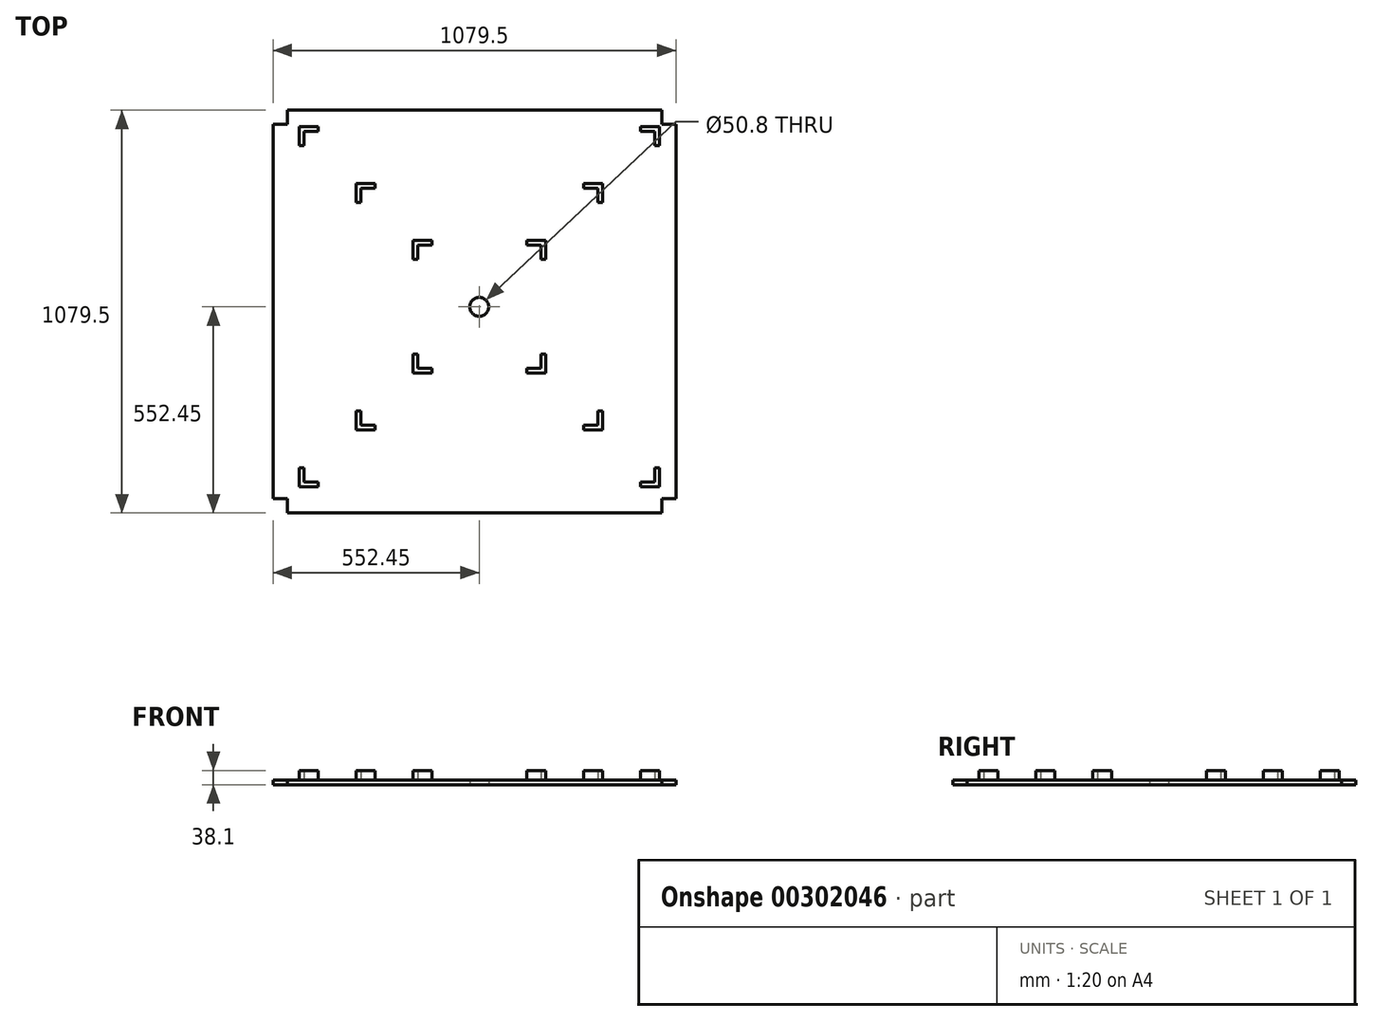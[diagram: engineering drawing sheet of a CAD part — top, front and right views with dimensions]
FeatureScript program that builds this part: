
annotation { "Feature Type Name" : "Feature", "Feature Type Description" : "" }
export const myFeature = defineFeature(function(context is Context, id is Id, definition is map)
    precondition{}
    {
        {
            var Q0;
            Q0=qCreatedBy(makeId("Top.planeOp"),FACE);
            var sketch = newSketch(context, id + "F0", { "sketchPlane" : qUnion([Q0])});
            skLineSegment(sketch, "E0", {"start": v(-552.45, 488.95) * mm, "end": v(-552.45, -514.35) * mm});
            skLineSegment(sketch, "E1", {"start": v(-552.45, -514.35) * mm, "end": v(-514.35, -514.35) * mm});
            skLineSegment(sketch, "E2", {"start": v(-514.35, -514.35) * mm, "end": v(-514.35, -552.45) * mm});
            skLineSegment(sketch, "E3", {"start": v(-514.35, -552.45) * mm, "end": v(488.95, -552.45) * mm});
            skLineSegment(sketch, "E4", {"start": v(488.95, -552.45) * mm, "end": v(488.95, -514.35) * mm});
            skLineSegment(sketch, "E5", {"start": v(488.95, -514.35) * mm, "end": v(527.05, -514.35) * mm});
            skLineSegment(sketch, "E6", {"start": v(527.05, -514.35) * mm, "end": v(527.05, 488.95) * mm});
            skLineSegment(sketch, "E7", {"start": v(527.05, 488.95) * mm, "end": v(488.95, 488.95) * mm});
            skLineSegment(sketch, "E8", {"start": v(488.95, 488.95) * mm, "end": v(488.95, 527.05) * mm});
            skLineSegment(sketch, "E9", {"start": v(488.95, 527.05) * mm, "end": v(-514.35, 527.05) * mm});
            skLineSegment(sketch, "E10", {"start": v(-514.35, 527.05) * mm, "end": v(-514.35, 488.95) * mm});
            skLineSegment(sketch, "E11", {"start": v(-514.35, 488.95) * mm, "end": v(-552.45, 488.95) * mm});
            skCircle(sketch, "E12", {"center": v(0, 0) * mm, "radius": 25.4 * mm});
            skSolve(sketch);
        }
        {
            var Q0;
            Q0=makeQuery(id+"F0.imprint","IMPRINT",FACE,{"disambiguationData":[TD([[makeQuery(id+"F0.imprint","IMPRINT",EDGE,{"derivedFrom":sQuery(id+"F0.wireOp",EDGE,"E0")}),1.0]])]});
            extrude(context, id + "F1", {"entities" : qUnion([Q0]), "depth" : 12.7 * mm});
        }
        {
            var Q0;
            Q0=makeQuery(id+"F1.opExtrude","CAP_FACE",FACE,{"disambiguationData":[OSD([sQuery(id+"F0.wireOp",EDGE,"E0"),sQuery(id+"F0.wireOp",EDGE,"E1"),sQuery(id+"F0.wireOp",EDGE,"E2"),sQuery(id+"F0.wireOp",EDGE,"E3"),sQuery(id+"F0.wireOp",EDGE,"E4"),sQuery(id+"F0.wireOp",EDGE,"E5"),sQuery(id+"F0.wireOp",EDGE,"E6"),sQuery(id+"F0.wireOp",EDGE,"E7"),sQuery(id+"F0.wireOp",EDGE,"E8"),sQuery(id+"F0.wireOp",EDGE,"E9"),sQuery(id+"F0.wireOp",EDGE,"E10"),sQuery(id+"F0.wireOp",EDGE,"E11"),sQuery(id+"F0.wireOp",EDGE,"E12")])],"isStart":false});
            var sketch = newSketch(context, id + "F2", { "sketchPlane" : qUnion([Q0])});
            skLineSegment(sketch, "E13", {"start": v(-482.6, 482.6) * mm, "end": v(-482.6, 431.8) * mm});
            skLineSegment(sketch, "E14", {"start": v(-482.6, 431.8) * mm, "end": v(-469.9, 431.8) * mm});
            skLineSegment(sketch, "E15", {"start": v(-469.9, 431.8) * mm, "end": v(-469.9, 469.9) * mm});
            skLineSegment(sketch, "E16", {"start": v(-469.9, 469.9) * mm, "end": v(-431.8, 469.9) * mm});
            skLineSegment(sketch, "E17", {"start": v(-431.8, 469.9) * mm, "end": v(-431.8, 482.6) * mm});
            skLineSegment(sketch, "E18", {"start": v(-431.8, 482.6) * mm, "end": v(-482.6, 482.6) * mm});
            skLineSegment(sketch, "E19", {"start": v(431.8, 482.6) * mm, "end": v(482.6, 482.6) * mm});
            skLineSegment(sketch, "E20", {"start": v(482.6, 482.6) * mm, "end": v(482.6, 431.8) * mm});
            skLineSegment(sketch, "E21", {"start": v(482.6, 431.8) * mm, "end": v(469.9, 431.8) * mm});
            skLineSegment(sketch, "E22", {"start": v(469.9, 431.8) * mm, "end": v(469.9, 469.9) * mm});
            skLineSegment(sketch, "E23", {"start": v(469.9, 469.9) * mm, "end": v(431.8, 469.9) * mm});
            skLineSegment(sketch, "E24", {"start": v(431.8, 469.9) * mm, "end": v(431.8, 482.6) * mm});
            skLineSegment(sketch, "E25", {"start": v(482.6, -482.6) * mm, "end": v(482.6, -431.8) * mm});
            skLineSegment(sketch, "E26", {"start": v(482.6, -431.8) * mm, "end": v(469.9, -431.8) * mm});
            skLineSegment(sketch, "E27", {"start": v(469.9, -431.8) * mm, "end": v(469.9, -469.9) * mm});
            skLineSegment(sketch, "E28", {"start": v(469.9, -469.9) * mm, "end": v(431.8, -469.9) * mm});
            skLineSegment(sketch, "E29", {"start": v(431.8, -469.9) * mm, "end": v(431.8, -482.6) * mm});
            skLineSegment(sketch, "E30", {"start": v(431.8, -482.6) * mm, "end": v(482.6, -482.6) * mm});
            skLineSegment(sketch, "E31", {"start": v(-482.6, -431.8) * mm, "end": v(-482.6, -482.6) * mm});
            skLineSegment(sketch, "E32", {"start": v(-482.6, -482.6) * mm, "end": v(-431.8, -482.6) * mm});
            skLineSegment(sketch, "E33", {"start": v(-431.8, -482.6) * mm, "end": v(-431.8, -469.9) * mm});
            skLineSegment(sketch, "E34", {"start": v(-431.8, -469.9) * mm, "end": v(-469.9, -469.9) * mm});
            skLineSegment(sketch, "E35", {"start": v(-469.9, -469.9) * mm, "end": v(-469.9, -431.8) * mm});
            skLineSegment(sketch, "E36", {"start": v(-469.9, -431.8) * mm, "end": v(-482.6, -431.8) * mm});
            skLineSegment(sketch, "E37", {"start": v(-330.2, -279.4) * mm, "end": v(-330.2, -330.2) * mm});
            skLineSegment(sketch, "E38", {"start": v(-330.2, -330.2) * mm, "end": v(-279.4, -330.2) * mm});
            skLineSegment(sketch, "E39", {"start": v(-279.4, -330.2) * mm, "end": v(-279.4, -317.5) * mm});
            skLineSegment(sketch, "E40", {"start": v(-279.4, -317.5) * mm, "end": v(-317.5, -317.5) * mm});
            skLineSegment(sketch, "E41", {"start": v(-317.5, -317.5) * mm, "end": v(-317.5, -279.4) * mm});
            skLineSegment(sketch, "E42", {"start": v(-317.5, -279.4) * mm, "end": v(-330.2, -279.4) * mm});
            skLineSegment(sketch, "E43", {"start": v(330.2, -279.4) * mm, "end": v(330.2, -330.2) * mm});
            skLineSegment(sketch, "E44", {"start": v(330.2, -330.2) * mm, "end": v(279.4, -330.2) * mm});
            skLineSegment(sketch, "E45", {"start": v(279.4, -330.2) * mm, "end": v(279.4, -317.5) * mm});
            skLineSegment(sketch, "E46", {"start": v(279.4, -317.5) * mm, "end": v(317.5, -317.5) * mm});
            skLineSegment(sketch, "E47", {"start": v(317.5, -317.5) * mm, "end": v(317.5, -279.4) * mm});
            skLineSegment(sketch, "E48", {"start": v(317.5, -279.4) * mm, "end": v(330.2, -279.4) * mm});
            skLineSegment(sketch, "E49", {"start": v(-177.8, -127) * mm, "end": v(-177.8, -177.8) * mm});
            skLineSegment(sketch, "E50", {"start": v(-177.8, -177.8) * mm, "end": v(-127, -177.8) * mm});
            skLineSegment(sketch, "E51", {"start": v(-127, -177.8) * mm, "end": v(-127, -165.1) * mm});
            skLineSegment(sketch, "E52", {"start": v(-127, -165.1) * mm, "end": v(-165.1, -165.1) * mm});
            skLineSegment(sketch, "E53", {"start": v(-165.1, -165.1) * mm, "end": v(-165.1, -127) * mm});
            skLineSegment(sketch, "E54", {"start": v(-165.1, -127) * mm, "end": v(-177.8, -127) * mm});
            skLineSegment(sketch, "E55", {"start": v(177.8, -127) * mm, "end": v(177.8, -177.8) * mm});
            skLineSegment(sketch, "E56", {"start": v(177.8, -177.8) * mm, "end": v(127, -177.8) * mm});
            skLineSegment(sketch, "E57", {"start": v(127, -177.8) * mm, "end": v(127, -165.1) * mm});
            skLineSegment(sketch, "E58", {"start": v(127, -165.1) * mm, "end": v(165.1, -165.1) * mm});
            skLineSegment(sketch, "E59", {"start": v(165.1, -165.1) * mm, "end": v(165.1, -127) * mm});
            skLineSegment(sketch, "E60", {"start": v(165.1, -127) * mm, "end": v(177.8, -127) * mm});
            skLineSegment(sketch, "E61", {"start": v(127, 177.8) * mm, "end": v(177.8, 177.8) * mm});
            skLineSegment(sketch, "E62", {"start": v(177.8, 177.8) * mm, "end": v(177.8, 127) * mm});
            skLineSegment(sketch, "E63", {"start": v(177.8, 127) * mm, "end": v(165.1, 127) * mm});
            skLineSegment(sketch, "E64", {"start": v(165.1, 127) * mm, "end": v(165.1, 165.1) * mm});
            skLineSegment(sketch, "E65", {"start": v(165.1, 165.1) * mm, "end": v(127, 165.1) * mm});
            skLineSegment(sketch, "E66", {"start": v(127, 165.1) * mm, "end": v(127, 177.8) * mm});
            skLineSegment(sketch, "E67", {"start": v(279.4, 330.2) * mm, "end": v(279.4, 317.5) * mm});
            skLineSegment(sketch, "E68", {"start": v(279.4, 317.5) * mm, "end": v(317.5, 317.5) * mm});
            skLineSegment(sketch, "E69", {"start": v(317.5, 317.5) * mm, "end": v(317.5, 279.4) * mm});
            skLineSegment(sketch, "E70", {"start": v(317.5, 279.4) * mm, "end": v(330.2, 279.4) * mm});
            skLineSegment(sketch, "E71", {"start": v(330.2, 279.4) * mm, "end": v(330.2, 330.2) * mm});
            skLineSegment(sketch, "E72", {"start": v(330.2, 330.2) * mm, "end": v(279.4, 330.2) * mm});
            skLineSegment(sketch, "E73", {"start": v(-330.2, 279.4) * mm, "end": v(-330.2, 330.2) * mm});
            skLineSegment(sketch, "E74", {"start": v(-330.2, 330.2) * mm, "end": v(-279.4, 330.2) * mm});
            skLineSegment(sketch, "E75", {"start": v(-279.4, 330.2) * mm, "end": v(-279.4, 317.5) * mm});
            skLineSegment(sketch, "E76", {"start": v(-279.4, 317.5) * mm, "end": v(-317.5, 317.5) * mm});
            skLineSegment(sketch, "E77", {"start": v(-317.5, 317.5) * mm, "end": v(-317.5, 279.4) * mm});
            skLineSegment(sketch, "E78", {"start": v(-317.5, 279.4) * mm, "end": v(-330.2, 279.4) * mm});
            skLineSegment(sketch, "E79", {"start": v(-177.8, 177.8) * mm, "end": v(-127, 177.8) * mm});
            skLineSegment(sketch, "E80", {"start": v(-127, 177.8) * mm, "end": v(-127, 165.1) * mm});
            skLineSegment(sketch, "E81", {"start": v(-127, 165.1) * mm, "end": v(-165.1, 165.1) * mm});
            skLineSegment(sketch, "E82", {"start": v(-165.1, 165.1) * mm, "end": v(-165.1, 127) * mm});
            skLineSegment(sketch, "E83", {"start": v(-165.1, 127) * mm, "end": v(-177.8, 127) * mm});
            skLineSegment(sketch, "E84", {"start": v(-177.8, 127) * mm, "end": v(-177.8, 177.8) * mm});
            skSolve(sketch);
        }
        {
            var Q0;
            Q0=makeQuery(id+"F2.imprint","IMPRINT",FACE,{"disambiguationData":[TD([[makeQuery(id+"F2.imprint","IMPRINT",EDGE,{"derivedFrom":sQuery(id+"F2.wireOp",EDGE,"E73")}),-1.0]])]});
            var Q1;
            Q1=makeQuery(id+"F2.imprint","IMPRINT",FACE,{"disambiguationData":[TD([[makeQuery(id+"F2.imprint","IMPRINT",EDGE,{"derivedFrom":sQuery(id+"F2.wireOp",EDGE,"E79")}),-1.0]])]});
            var Q2;
            Q2=makeQuery(id+"F2.imprint","IMPRINT",FACE,{"disambiguationData":[TD([[makeQuery(id+"F2.imprint","IMPRINT",EDGE,{"derivedFrom":sQuery(id+"F2.wireOp",EDGE,"E49")}),1.0]])]});
            var Q3;
            Q3=makeQuery(id+"F2.imprint","IMPRINT",FACE,{"disambiguationData":[TD([[makeQuery(id+"F2.imprint","IMPRINT",EDGE,{"derivedFrom":sQuery(id+"F2.wireOp",EDGE,"E61")}),-1.0]])]});
            var Q4;
            Q4=makeQuery(id+"F2.imprint","IMPRINT",FACE,{"disambiguationData":[TD([[makeQuery(id+"F2.imprint","IMPRINT",EDGE,{"derivedFrom":sQuery(id+"F2.wireOp",EDGE,"E67")}),1.0]])]});
            var Q5;
            Q5=makeQuery(id+"F2.imprint","IMPRINT",FACE,{"disambiguationData":[TD([[makeQuery(id+"F2.imprint","IMPRINT",EDGE,{"derivedFrom":sQuery(id+"F2.wireOp",EDGE,"E55")}),-1.0]])]});
            var Q6;
            Q6=makeQuery(id+"F2.imprint","IMPRINT",FACE,{"disambiguationData":[TD([[makeQuery(id+"F2.imprint","IMPRINT",EDGE,{"derivedFrom":sQuery(id+"F2.wireOp",EDGE,"E19")}),-1.0]])]});
            var Q7;
            Q7=makeQuery(id+"F2.imprint","IMPRINT",FACE,{"disambiguationData":[TD([[makeQuery(id+"F2.imprint","IMPRINT",EDGE,{"derivedFrom":sQuery(id+"F2.wireOp",EDGE,"E13")}),1.0]])]});
            var Q8;
            Q8=makeQuery(id+"F2.imprint","IMPRINT",FACE,{"disambiguationData":[TD([[makeQuery(id+"F2.imprint","IMPRINT",EDGE,{"derivedFrom":sQuery(id+"F2.wireOp",EDGE,"E37")}),1.0]])]});
            var Q9;
            Q9=makeQuery(id+"F2.imprint","IMPRINT",FACE,{"disambiguationData":[TD([[makeQuery(id+"F2.imprint","IMPRINT",EDGE,{"derivedFrom":sQuery(id+"F2.wireOp",EDGE,"E31")}),1.0]])]});
            var Q10;
            Q10=makeQuery(id+"F2.imprint","IMPRINT",FACE,{"disambiguationData":[TD([[makeQuery(id+"F2.imprint","IMPRINT",EDGE,{"derivedFrom":sQuery(id+"F2.wireOp",EDGE,"E43")}),-1.0]])]});
            var Q11;
            Q11=makeQuery(id+"F2.imprint","IMPRINT",FACE,{"disambiguationData":[TD([[makeQuery(id+"F2.imprint","IMPRINT",EDGE,{"derivedFrom":sQuery(id+"F2.wireOp",EDGE,"E25")}),1.0]])]});
            extrude(context, id + "F3", {"entities" : qUnion([Q0, Q1, Q2, Q3, Q4, Q5, Q6, Q7, Q8, Q9, Q10, Q11]), "operationType" : NewBodyOperationType.ADD, "depth" : 25.4 * mm});
        }
    });
